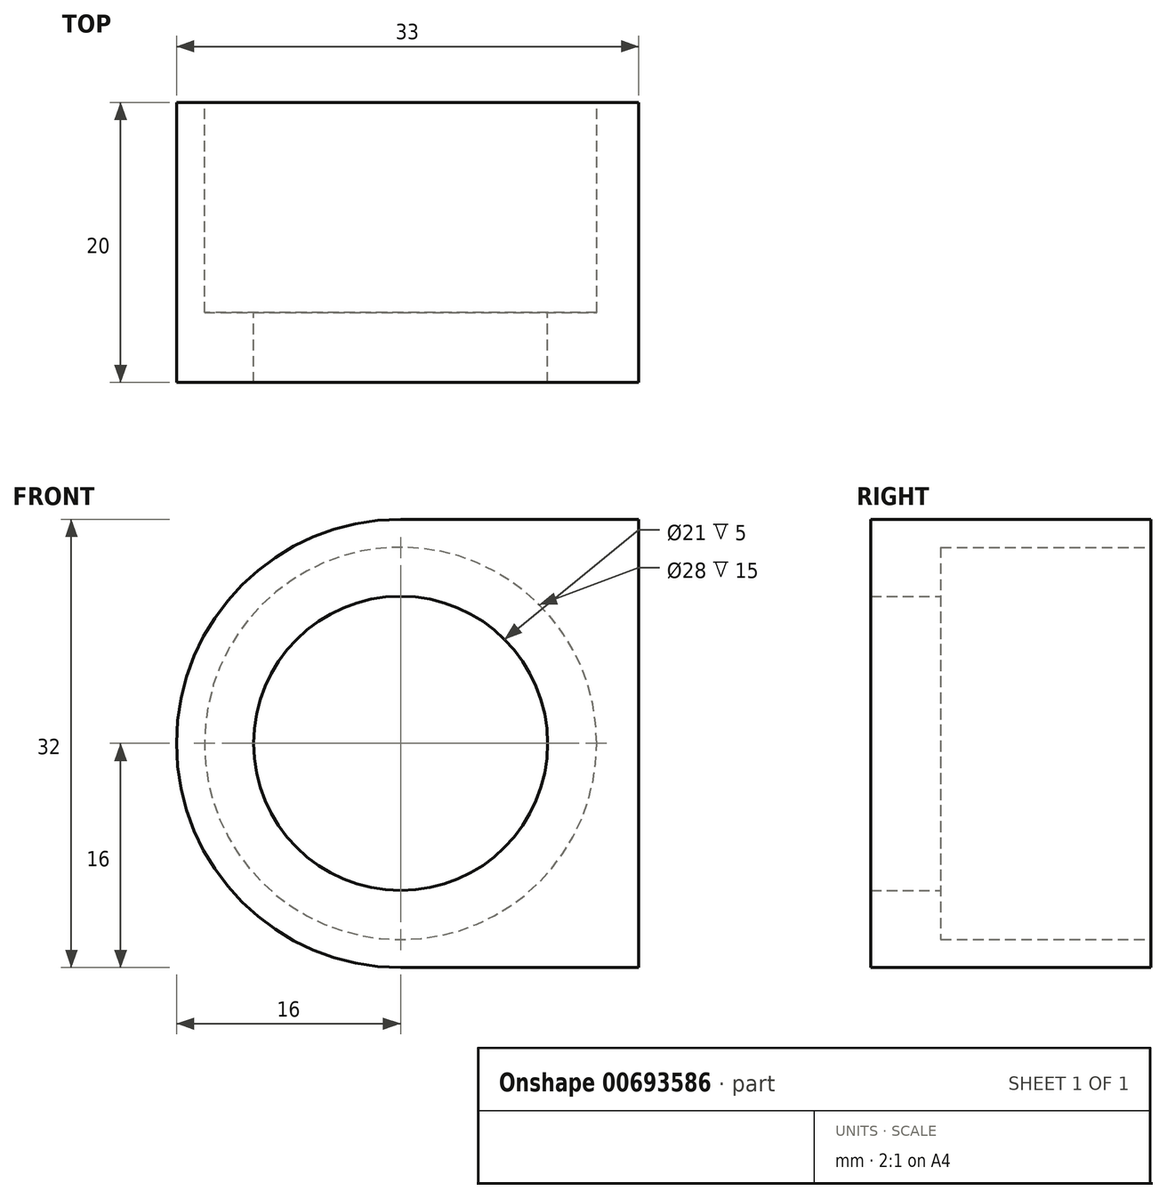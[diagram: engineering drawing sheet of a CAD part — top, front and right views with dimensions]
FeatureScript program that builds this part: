
annotation { "Feature Type Name" : "Feature", "Feature Type Description" : "" }
export const myFeature = defineFeature(function(context is Context, id is Id, definition is map)
    precondition{}
    {
        {
            var Q0;
            Q0=qCreatedBy(makeId("Front.planeOp"),FACE);
            var sketch = newSketch(context, id + "F0", { "sketchPlane" : qUnion([Q0])});
            skCircle(sketch, "E0", {"center": v(0, 0) * mm, "radius": 16 * mm});
            skCircle(sketch, "E1", {"center": v(0, 0) * mm, "radius": 10.5 * mm});
            skSolve(sketch);
        }
        {
            var Q0;
            Q0 = qSketchRegion(id + "F0", true);
            extrude(context, id + "F1", {"entities" : qUnion([Q0]), "depth" : 20 * mm, "offsetDistance" : 25 * mm});
        }
        {
            var Q0;
            Q0=makeQuery(id+"F1.opExtrude","CAP_FACE",FACE,{"disambiguationData":[OSD([sQuery(id+"F0.wireOp",EDGE,"E0"),sQuery(id+"F0.wireOp",EDGE,"E1")])],"isStart":false});
            var sketch = newSketch(context, id + "F2", { "sketchPlane" : qUnion([Q0])});
            skCircle(sketch, "E2", {"center": v(0, 0) * mm, "radius": 12.5 * mm});
            skSolve(sketch);
        }
        {
            var Q0;
            Q0 = qSketchRegion(id + "F2", true);
            extrude(context, id + "F3", {"entities" : qUnion([Q0]), "operationType" : NewBodyOperationType.ADD, "oppositeDirection" : true, "depth" : 15 * mm, "offsetDistance" : 25 * mm});
        }
        {
            var Q0;
            Q0=makeQuery(id+"F3.opExtrude","CAP_FACE",FACE,{"disambiguationData":[OSD([sQuery(id+"F2.wireOp",EDGE,"E2")])],"isStart":false});
            extrude(context, id + "F4", {"entities" : qUnion([Q0]), "operationType" : NewBodyOperationType.REMOVE, "endBound" : BoundingType.THROUGH_ALL, "oppositeDirection" : true, "depth" : 25 * mm, "offsetDistance" : 25 * mm});
        }
        {
            var Q0;
            Q0=makeQuery(id+"F1.opExtrude","CAP_FACE",FACE,{"disambiguationData":[OSD([sQuery(id+"F0.wireOp",EDGE,"E0"),sQuery(id+"F0.wireOp",EDGE,"E1")])],"isStart":true});
            var sketch = newSketch(context, id + "F5", { "sketchPlane" : qUnion([Q0])});
            skCircle(sketch, "E3", {"center": v(0, 0) * mm, "radius": 14 * mm});
            skSolve(sketch);
        }
        {
            var Q0;
            Q0 = qSketchRegion(id + "F5", true);
            extrude(context, id + "F6", {"entities" : qUnion([Q0]), "operationType" : NewBodyOperationType.REMOVE, "oppositeDirection" : true, "depth" : 15 * mm, "offsetDistance" : 25 * mm});
        }
        {
            var Q0;
            Q0=qCreatedBy(makeId("Right.planeOp"),FACE);
            cPlane(context, id + "F7", {"entities" : qUnion([Q0]), "cplaneType" : CPlaneType.OFFSET, "offset" : 15 * mm, "width" : 150 * mm, "height" : 150 * mm});
        }
        {
            var Q0;
            Q0=qCreatedBy(id+"F7.planeOp",FACE);
            var sketch = newSketch(context, id + "F8", { "sketchPlane" : qUnion([Q0])});
            skLineSegment(sketch, "E4.bottom", {"start": v(0, 0) * mm, "end": v(-20, 0) * mm});
            skLineSegment(sketch, "E4.top", {"start": v(0, 16) * mm, "end": v(-20, 16) * mm});
            skLineSegment(sketch, "E4.left", {"start": v(0, 0) * mm, "end": v(0, 16) * mm});
            skLineSegment(sketch, "E4.right", {"start": v(-20, 0) * mm, "end": v(-20, 16) * mm});
            skLineSegment(sketch, "E5.top", {"start": v(0, -16) * mm, "end": v(-20, -16) * mm});
            skLineSegment(sketch, "E5.left", {"start": v(0, 0) * mm, "end": v(0, -16) * mm});
            skLineSegment(sketch, "E5.right", {"start": v(-20, 0) * mm, "end": v(-20, -16) * mm});
            skSolve(sketch);
        }
        {
            var Q0;
            Q0 = qSketchRegion(id + "F8", true);
            extrude(context, id + "F9", {"entities" : qUnion([Q0]), "operationType" : NewBodyOperationType.ADD, "depth" : 2 * mm, "offsetDistance" : 25 * mm});
        }
        {
            var Q0;
            Q0=makeQuery(id+"F3.boolean.opBoolean","MERGE",FACE,{"derivedFrom":[makeQuery(id+"F1.opExtrude","CAP_FACE",FACE,{"disambiguationData":[OSD([sQuery(id+"F0.wireOp",EDGE,"E0"),sQuery(id+"F0.wireOp",EDGE,"E1")])],"isStart":false}),makeQuery(id+"F3.opExtrude","CAP_FACE",FACE,{"disambiguationData":[OSD([sQuery(id+"F2.wireOp",EDGE,"E2")])],"isStart":true})]});
            var sketch = newSketch(context, id + "F10", { "sketchPlane" : qUnion([Q0])});
            skLineSegment(sketch, "E6", {"start": v(0, 16) * mm, "end": v(15.98, 16) * mm});
            skLineSegment(sketch, "E7", {"start": v(0, -16) * mm, "end": v(16.04, -16) * mm});
            skSolve(sketch);
        }
        {
            var Q0;
            {var subQ1=sQuery(id+"F8.wireOp",EDGE,"E4.top");var subQ3=sQuery(id+"F8.wireOp",EDGE,"E5.right");var subQ4=sQuery(id+"F8.wireOp",EDGE,"E4.right");var subQ5=makeQuery(id+"F9.boolean.opBoolean","SPLIT",EDGE,{"disambiguationData":[TD([makeQuery(id+"F9.opExtrude","SWEPT_FACE",FACE,{"disambiguationData":[OSD([subQ1])]})])],"derivedFrom":makeQuery(id+"F9.opExtrude","CAP_EDGE",EDGE,{"disambiguationData":[OSD([subQ4,subQ3])],"isStart":true})});Q0=makeQuery(id+"F10.imprint","IMPRINT",FACE,{"disambiguationData":[TD([[makeQuery(id+"F10.imprint","IMPRINT",EDGE,{"derivedFrom":subQ5}),1.0]])]});}
            extrude(context, id + "F11", {"entities" : qUnion([Q0]), "operationType" : NewBodyOperationType.ADD, "oppositeDirection" : true, "depth" : 20 * mm, "offsetDistance" : 25 * mm});
        }
        {
            var Q0;
            {var subQ0=sQuery(id+"F8.wireOp",EDGE,"E5.right");var subQ1=sQuery(id+"F8.wireOp",EDGE,"E4.right");var subQ2=sQuery(id+"F0.wireOp",EDGE,"E0");Q0=makeQuery(id+"F11.boolean.opBoolean","MERGE",FACE,{"derivedFrom":[makeQuery(id+"F9.boolean.opBoolean","MERGE",FACE,{"derivedFrom":[makeQuery(id+"F3.boolean.opBoolean","MERGE",FACE,{"derivedFrom":[makeQuery(id+"F1.opExtrude","CAP_FACE",FACE,{"disambiguationData":[OSD([subQ2,sQuery(id+"F0.wireOp",EDGE,"E1")])],"isStart":false}),makeQuery(id+"F3.opExtrude","CAP_FACE",FACE,{"disambiguationData":[OSD([sQuery(id+"F2.wireOp",EDGE,"E2")])],"isStart":true})]}),makeQuery(id+"F9.opExtrude","SWEPT_FACE",FACE,{"disambiguationData":[OSD([subQ1,subQ0])]})]}),makeQuery(id+"F11.opExtrude","CAP_FACE",FACE,{"disambiguationData":[OSD([subQ2,subQ1,subQ0,sQuery(id+"F10.wireOp",EDGE,"E6")])],"isStart":true})]});}
            var sketch = newSketch(context, id + "F12", { "sketchPlane" : qUnion([Q0])});
            skSolve(sketch);
        }
        {
            var Q0;
            {var subQ3=sQuery(id+"F0.wireOp",EDGE,"E0");Q0=makeQuery(id+"F12.imprint","IMPRINT",FACE,{"disambiguationData":[TD([[makeQuery(id+"F12.imprint","IMPRINT",EDGE,{"derivedFrom":makeQuery(id+"F1.opExtrude","CAP_EDGE",EDGE,{"disambiguationData":[OSD([subQ3])],"isStart":false})}),1.0]])]});}
            var sketch = newSketch(context, id + "F13", { "sketchPlane" : qUnion([Q0])});
            skLineSegment(sketch, "E8", {"start": v(15, -16) * mm, "end": v(0, -16) * mm});
            skSolve(sketch);
        }
        {
            var Q0;
            Q0 = qSketchRegion(id + "F13", true);
            var Q1;
            {var subQ0=sQuery(id+"F13.wireOp",EDGE,"E8");Q1=makeQuery(id+"F13.imprint","IMPRINT",FACE,{"disambiguationData":[TD([[makeQuery(id+"F13.imprint","IMPRINT",EDGE,{"derivedFrom":subQ0}),-1.0]])]});}
            extrude(context, id + "F14", {"entities" : qUnion([Q0, Q1]), "operationType" : NewBodyOperationType.ADD, "oppositeDirection" : true, "depth" : 20 * mm, "offsetDistance" : 25 * mm});
        }
    });
